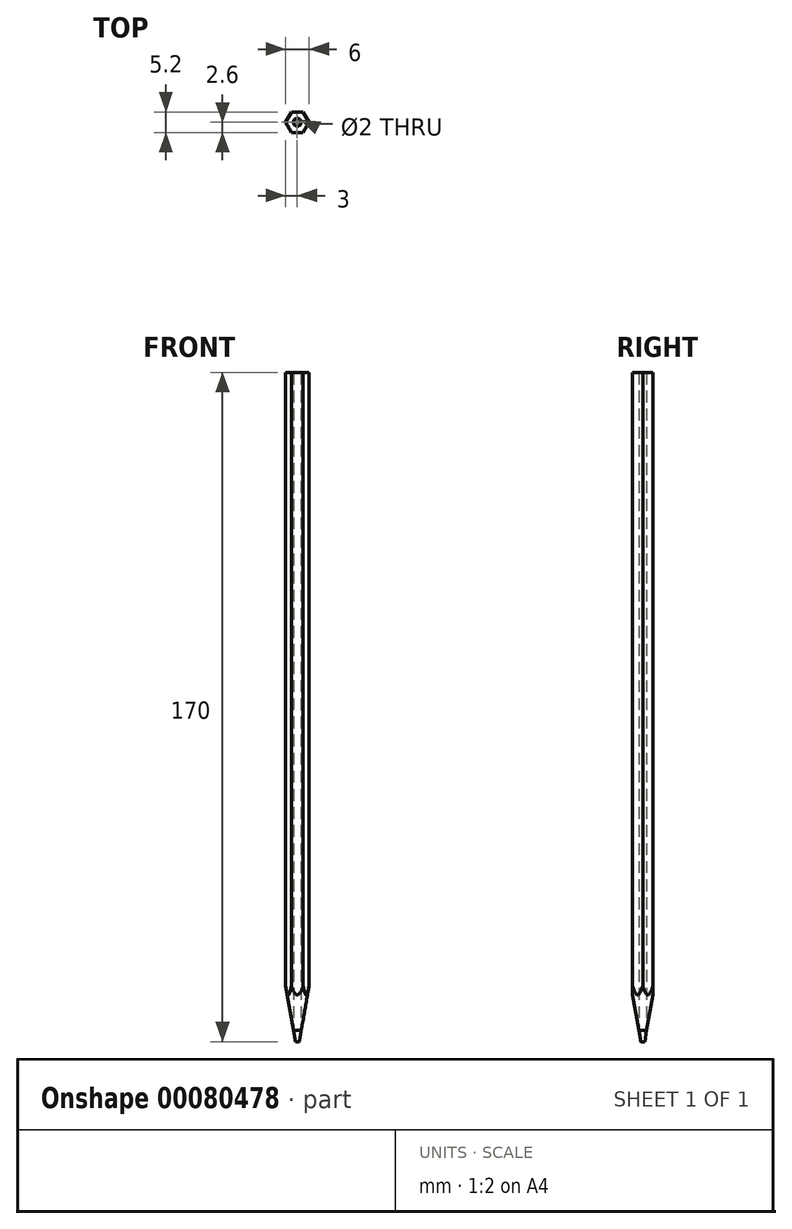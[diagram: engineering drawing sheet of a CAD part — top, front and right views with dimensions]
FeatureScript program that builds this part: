
annotation { "Feature Type Name" : "Feature", "Feature Type Description" : "" }
export const myFeature = defineFeature(function(context is Context, id is Id, definition is map)
    precondition{}
    {
        {
            var Q0;
            Q0=qCreatedBy(makeId("Top.planeOp"),FACE);
            var sketch = newSketch(context, id + "F0", { "sketchPlane" : qUnion([Q0])});
            skCircle(sketch, "E0.cCircle", {"center": v(0, 0) * mm, "radius": 3 * mm, "construction": true});
            skLineSegment(sketch, "E0.0", {"start": v(-1.5, 2.6) * mm, "end": v(1.5, 2.6) * mm});
            skLineSegment(sketch, "E0.1", {"start": v(1.5, 2.6) * mm, "end": v(3, 0) * mm});
            skLineSegment(sketch, "E0.2", {"start": v(3, 0) * mm, "end": v(1.5, -2.6) * mm});
            skLineSegment(sketch, "E0.3", {"start": v(1.5, -2.6) * mm, "end": v(-1.5, -2.6) * mm});
            skLineSegment(sketch, "E0.4", {"start": v(-1.5, -2.6) * mm, "end": v(-3, 0) * mm});
            skLineSegment(sketch, "E0.5", {"start": v(-3, 0) * mm, "end": v(-1.5, 2.6) * mm});
            skCircle(sketch, "E1", {"center": v(0, 0) * mm, "radius": 1 * mm});
            skSolve(sketch);
        }
        {
            var Q0;
            Q0 = qSketchRegion(id + "F0", true);
            extrude(context, id + "F1", {"entities" : qUnion([Q0]), "depth" : 170 * mm});
        }
        {
            var Q0;
            Q0=makeQuery(id+"F0.imprint","IMPRINT",FACE,{"disambiguationData":[TD([[makeQuery(id+"F0.imprint","IMPRINT",EDGE,{"derivedFrom":sQuery(id+"F0.wireOp",EDGE,"E1")}),1.0]])]});
            extrude(context, id + "F2", {"entities" : qUnion([Q0]), "depth" : 170 * mm});
        }
        {
            var Q0;
            Q0=qCreatedBy(makeId("Front.planeOp"),FACE);
            var sketch = newSketch(context, id + "F3", { "sketchPlane" : qUnion([Q0])});
            skLineSegment(sketch, "E2", {"start": v(0.5, 0) * mm, "end": v(3.64, 17.8) * mm});
            skLineSegment(sketch, "E3", {"start": v(3.64, 17.8) * mm, "end": v(3.64, 0) * mm});
            skLineSegment(sketch, "E4", {"start": v(3.64, 0) * mm, "end": v(0.5, 0) * mm});
            skLineSegment(sketch, "E5", {"start": v(0, 0) * mm, "end": v(0, -7.98) * mm, "construction": true});
            skSolve(sketch);
        }
        {
            var Q0;
            Q0 = qSketchRegion(id + "F3", true);
            var Q1;
            Q1=sQuery(id+"F3.wireOp",EDGE,"E5");
            revolve(context, id + "F4", {"operationType" : NewBodyOperationType.REMOVE, "entities" : qUnion([Q0]), "axis" : qUnion([Q1]), "revolveType" : RevolveType.FULL, "oppositeDirection" : true});
        }
    });
